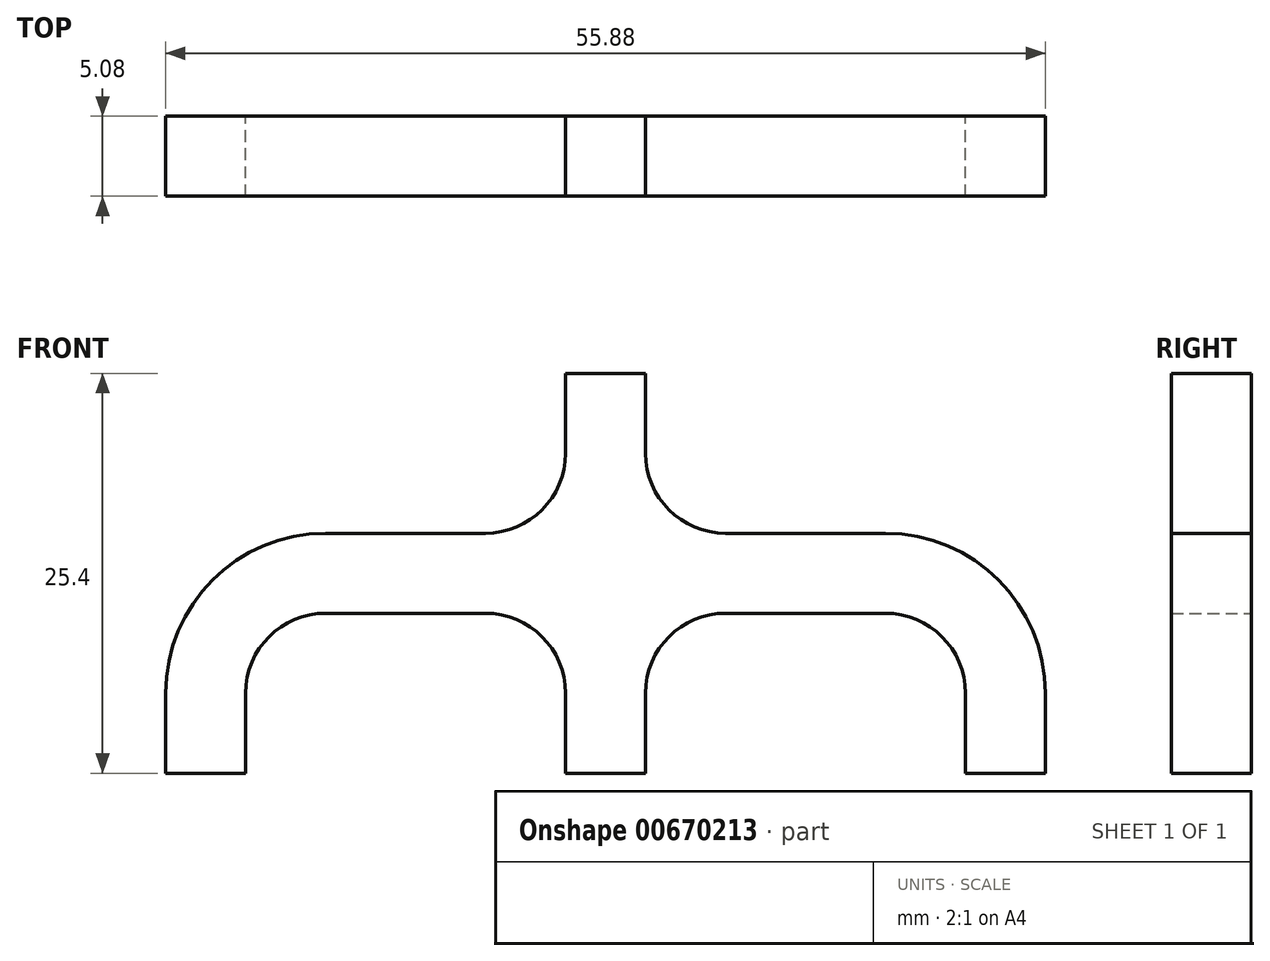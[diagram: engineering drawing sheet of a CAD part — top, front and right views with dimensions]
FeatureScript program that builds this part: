
annotation { "Feature Type Name" : "Feature", "Feature Type Description" : "" }
export const myFeature = defineFeature(function(context is Context, id is Id, definition is map)
    precondition{}
    {
        {
            var Q0;
            Q0=qCreatedBy(makeId("Front.planeOp"),FACE);
            var sketch = newSketch(context, id + "F0", { "sketchPlane" : qUnion([Q0])});
            skLineSegment(sketch, "E0", {"start": v(0, 0) * mm, "end": v(0, 25.4) * mm, "construction": true});
            skLineSegment(sketch, "E1", {"start": v(0, 12.7) * mm, "end": v(-25.4, 12.7) * mm, "construction": true});
            skLineSegment(sketch, "E2", {"start": v(-25.4, 12.7) * mm, "end": v(-25.4, 0) * mm, "construction": true});
            skLineSegment(sketch, "E3", {"start": v(0, 12.7) * mm, "end": v(25.4, 12.7) * mm, "construction": true});
            skLineSegment(sketch, "E4", {"start": v(25.4, 12.7) * mm, "end": v(25.4, 0) * mm, "construction": true});
            skLineSegment(sketch, "E5", {"start": v(-22.86, 0) * mm, "end": v(-27.94, 0) * mm});
            skLineSegment(sketch, "E6", {"start": v(-27.94, 0) * mm, "end": v(-27.94, 15.24) * mm});
            skLineSegment(sketch, "E7", {"start": v(-27.94, 15.24) * mm, "end": v(-2.54, 15.24) * mm});
            skLineSegment(sketch, "E8", {"start": v(-2.54, 15.24) * mm, "end": v(-2.54, 25.4) * mm});
            skLineSegment(sketch, "E9", {"start": v(-2.54, 25.4) * mm, "end": v(2.54, 25.4) * mm});
            skLineSegment(sketch, "E10", {"start": v(2.54, 25.4) * mm, "end": v(2.54, 15.24) * mm});
            skLineSegment(sketch, "E11", {"start": v(2.54, 15.24) * mm, "end": v(27.94, 15.24) * mm});
            skLineSegment(sketch, "E12", {"start": v(27.94, 15.24) * mm, "end": v(27.94, 0) * mm});
            skLineSegment(sketch, "E13", {"start": v(27.94, 0) * mm, "end": v(22.86, 0) * mm});
            skLineSegment(sketch, "E14", {"start": v(22.86, 0) * mm, "end": v(22.86, 10.16) * mm});
            skLineSegment(sketch, "E15", {"start": v(22.86, 10.16) * mm, "end": v(2.54, 10.16) * mm});
            skLineSegment(sketch, "E16", {"start": v(2.54, 10.16) * mm, "end": v(2.54, 0) * mm});
            skLineSegment(sketch, "E17", {"start": v(2.54, 0) * mm, "end": v(-2.54, 0) * mm});
            skLineSegment(sketch, "E18", {"start": v(-2.54, 0) * mm, "end": v(-2.54, 10.16) * mm});
            skLineSegment(sketch, "E19", {"start": v(-2.54, 10.16) * mm, "end": v(-22.86, 10.16) * mm});
            skLineSegment(sketch, "E20", {"start": v(-22.86, 10.16) * mm, "end": v(-22.86, 0) * mm});
            skSolve(sketch);
        }
        {
            var Q0;
            Q0=makeQuery(id+"F0.imprint","IMPRINT",FACE,{"disambiguationData":[TD([[makeQuery(id+"F0.imprint","IMPRINT",EDGE,{"derivedFrom":sQuery(id+"F0.wireOp",EDGE,"E5")}),-1.0]])]});
            extrude(context, id + "F1", {"entities" : qUnion([Q0]), "endBound" : BoundingType.SYMMETRIC, "depth" : 5.08 * mm, "offsetDistance" : 25.4 * mm});
        }
        {
            var Q0;
            Q0=makeQuery(id+"F1.opExtrude","SWEPT_EDGE",EDGE,{"disambiguationData":[OSD([sQuery(id+"F0.wireOp",EDGE,"E10"),sQuery(id+"F0.wireOp",EDGE,"E11")])]});
            var Q1;
            Q1=makeQuery(id+"F1.opExtrude","SWEPT_EDGE",EDGE,{"disambiguationData":[OSD([sQuery(id+"F0.wireOp",EDGE,"E15"),sQuery(id+"F0.wireOp",EDGE,"E16")])]});
            var Q2;
            Q2=makeQuery(id+"F1.opExtrude","SWEPT_EDGE",EDGE,{"disambiguationData":[OSD([sQuery(id+"F0.wireOp",EDGE,"E18"),sQuery(id+"F0.wireOp",EDGE,"E19")])]});
            var Q3;
            Q3=makeQuery(id+"F1.opExtrude","SWEPT_EDGE",EDGE,{"disambiguationData":[OSD([sQuery(id+"F0.wireOp",EDGE,"E7"),sQuery(id+"F0.wireOp",EDGE,"E8")])]});
            var Q4;
            Q4=makeQuery(id+"F1.opExtrude","SWEPT_EDGE",EDGE,{"disambiguationData":[OSD([sQuery(id+"F0.wireOp",EDGE,"E14"),sQuery(id+"F0.wireOp",EDGE,"E15")])]});
            var Q5;
            Q5=makeQuery(id+"F1.opExtrude","SWEPT_EDGE",EDGE,{"disambiguationData":[OSD([sQuery(id+"F0.wireOp",EDGE,"E19"),sQuery(id+"F0.wireOp",EDGE,"E20")])]});
            fillet(context, id + "F2", {"entities" : qUnion([Q0, Q1, Q2, Q3, Q4, Q5]), "radius" : 5.08 * mm, "tangentPropagation" : true, "allowEdgeOverflow" : false});
        }
        {
            var Q0;
            Q0=makeQuery(id+"F1.opExtrude","SWEPT_EDGE",EDGE,{"disambiguationData":[OSD([sQuery(id+"F0.wireOp",EDGE,"E11"),sQuery(id+"F0.wireOp",EDGE,"E12")])]});
            var Q1;
            Q1=makeQuery(id+"F1.opExtrude","SWEPT_EDGE",EDGE,{"disambiguationData":[OSD([sQuery(id+"F0.wireOp",EDGE,"E6"),sQuery(id+"F0.wireOp",EDGE,"E7")])]});
            fillet(context, id + "F3", {"entities" : qUnion([Q0, Q1]), "radius" : 10.16 * mm, "tangentPropagation" : true, "allowEdgeOverflow" : false});
        }
    });
